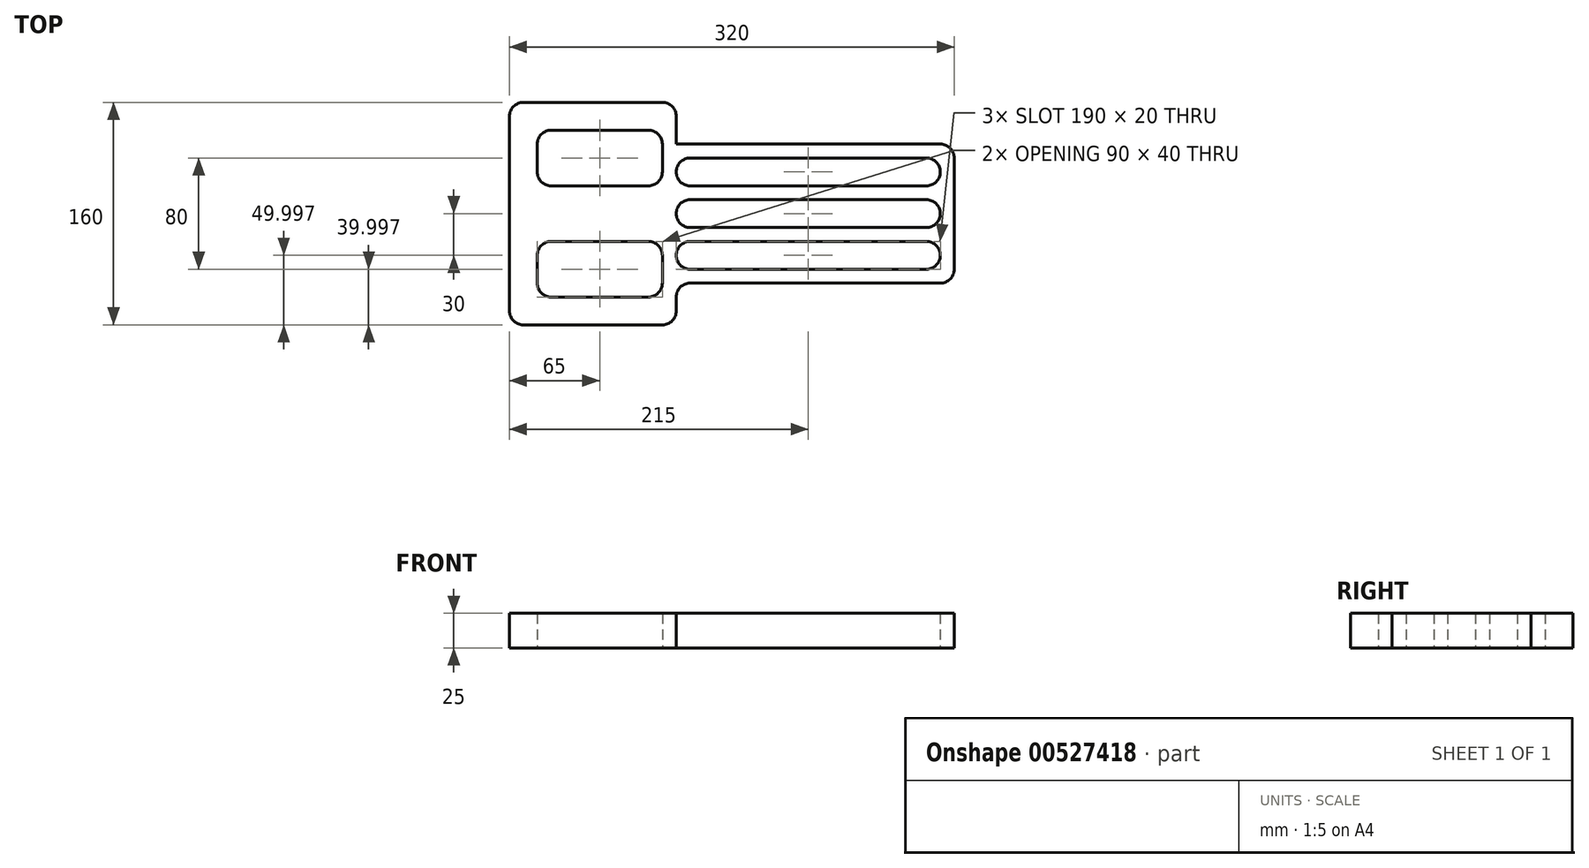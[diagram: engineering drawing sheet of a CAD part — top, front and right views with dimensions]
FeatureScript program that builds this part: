
annotation { "Feature Type Name" : "Feature", "Feature Type Description" : "" }
export const myFeature = defineFeature(function(context is Context, id is Id, definition is map)
    precondition{}
    {
        {
            var Q0;
            Q0=qCreatedBy(makeId("Top.planeOp"),FACE);
            var sketch = newSketch(context, id + "F0", { "sketchPlane" : qUnion([Q0])});
            skLineSegment(sketch, "E0", {"start": v(-100, 104.57) * mm, "end": v(0, 104.57) * mm});
            skLineSegment(sketch, "E1", {"start": v(-110, 94.57) * mm, "end": v(-110, -45.43) * mm});
            skLineSegment(sketch, "E2", {"start": v(-100, -55.43) * mm, "end": v(0, -55.43) * mm});
            skLineSegment(sketch, "E3", {"start": v(10, 94.57) * mm, "end": v(10, 74.57) * mm});
            skLineSegment(sketch, "E4", {"start": v(10, -45.43) * mm, "end": v(10, -35.43) * mm});
            skLineSegment(sketch, "E5", {"start": v(20, -25.43) * mm, "end": v(200, -25.43) * mm});
            skLineSegment(sketch, "E6", {"start": v(10, 74.57) * mm, "end": v(200, 74.57) * mm});
            skLineSegment(sketch, "E7", {"start": v(210, 64.57) * mm, "end": v(210, -15.43) * mm});
            skLineSegment(sketch, "E8.bottom", {"start": v(190, 44.57) * mm, "end": v(20, 44.57) * mm});
            skLineSegment(sketch, "E8.top", {"start": v(190, 64.57) * mm, "end": v(20, 64.57) * mm});
            skLineSegment(sketch, "E8.left", {"start": v(200, 54.57) * mm, "end": v(200, 54.57) * mm});
            skLineSegment(sketch, "E8.right", {"start": v(10, 54.57) * mm, "end": v(10, 54.57) * mm});
            skPoint(sketch, "E8.middle", {"position": v(105, 54.57) * mm});
            skLineSegment(sketch, "E9.bottom", {"start": v(190, 14.57) * mm, "end": v(20, 14.57) * mm});
            skLineSegment(sketch, "E9.top", {"start": v(190, 34.57) * mm, "end": v(20, 34.57) * mm});
            skLineSegment(sketch, "E9.left", {"start": v(200, 24.57) * mm, "end": v(200, 24.57) * mm});
            skLineSegment(sketch, "E9.right", {"start": v(10, 24.57) * mm, "end": v(10, 24.57) * mm});
            skPoint(sketch, "E9.middle", {"position": v(105, 24.57) * mm});
            skLineSegment(sketch, "E10.bottom", {"start": v(190, -15.43) * mm, "end": v(20, -15.43) * mm});
            skLineSegment(sketch, "E10.top", {"start": v(190, 4.57) * mm, "end": v(20, 4.57) * mm});
            skLineSegment(sketch, "E10.left", {"start": v(200, -5.43) * mm, "end": v(200, -5.43) * mm});
            skLineSegment(sketch, "E10.right", {"start": v(10, -5.43) * mm, "end": v(10, -5.43) * mm});
            skPoint(sketch, "E10.middle", {"position": v(105, -5.43) * mm});
            skLineSegment(sketch, "E11.bottom", {"start": v(-10, 84.57) * mm, "end": v(-80, 84.57) * mm});
            skLineSegment(sketch, "E11.top", {"start": v(-10, 44.57) * mm, "end": v(-80, 44.57) * mm});
            skLineSegment(sketch, "E11.left", {"start": v(0, 74.57) * mm, "end": v(0, 54.57) * mm});
            skLineSegment(sketch, "E11.right", {"start": v(-90, 74.57) * mm, "end": v(-90, 54.57) * mm});
            skPoint(sketch, "E11.middle", {"position": v(-45, 64.57) * mm});
            skLineSegment(sketch, "E12.bottom", {"start": v(-10, 4.57) * mm, "end": v(-80, 4.57) * mm});
            skLineSegment(sketch, "E12.top", {"start": v(-10, -35.43) * mm, "end": v(-80, -35.43) * mm});
            skLineSegment(sketch, "E12.left", {"start": v(0, -5.43) * mm, "end": v(0, -25.43) * mm});
            skLineSegment(sketch, "E12.right", {"start": v(-90, -5.43) * mm, "end": v(-90, -25.43) * mm});
            skPoint(sketch, "E12.middle", {"position": v(-45, -15.43) * mm});
            skPoint(sketch, "E13.visualSharp", {"position": v(10, 64.57) * mm});
            skArc(sketch, "E13.filletArc", {"start": v(20, 64.57) * mm, "mid": v(12.93, 61.64) * mm, "end": v(10, 54.57) * mm});
            skPoint(sketch, "E14.visualSharp", {"position": v(10, 44.57) * mm});
            skArc(sketch, "E14.filletArc", {"start": v(10, 54.57) * mm, "mid": v(12.93, 47.5) * mm, "end": v(20, 44.57) * mm});
            skPoint(sketch, "E15.visualSharp", {"position": v(10, 34.57) * mm});
            skArc(sketch, "E15.filletArc", {"start": v(20, 34.57) * mm, "mid": v(12.93, 31.64) * mm, "end": v(10, 24.57) * mm});
            skPoint(sketch, "E16.visualSharp", {"position": v(10, 14.57) * mm});
            skArc(sketch, "E16.filletArc", {"start": v(10, 24.57) * mm, "mid": v(12.93, 17.5) * mm, "end": v(20, 14.57) * mm});
            skPoint(sketch, "E17.visualSharp", {"position": v(10, 4.57) * mm});
            skArc(sketch, "E17.filletArc", {"start": v(20, 4.57) * mm, "mid": v(12.93, 1.64) * mm, "end": v(10, -5.43) * mm});
            skPoint(sketch, "E18.visualSharp", {"position": v(10, -15.43) * mm});
            skArc(sketch, "E18.filletArc", {"start": v(10, -5.43) * mm, "mid": v(12.93, -12.5) * mm, "end": v(20, -15.43) * mm});
            skPoint(sketch, "E19.visualSharp", {"position": v(200, 4.57) * mm});
            skArc(sketch, "E19.filletArc", {"start": v(200, -5.43) * mm, "mid": v(197.07, 1.64) * mm, "end": v(190, 4.57) * mm});
            skPoint(sketch, "E20.visualSharp", {"position": v(200, -15.43) * mm});
            skArc(sketch, "E20.filletArc", {"start": v(190, -15.43) * mm, "mid": v(197.07, -12.5) * mm, "end": v(200, -5.43) * mm});
            skPoint(sketch, "E21.visualSharp", {"position": v(200, 34.57) * mm});
            skArc(sketch, "E21.filletArc", {"start": v(200, 24.57) * mm, "mid": v(197.07, 31.64) * mm, "end": v(190, 34.57) * mm});
            skPoint(sketch, "E22.visualSharp", {"position": v(200, 14.57) * mm});
            skArc(sketch, "E22.filletArc", {"start": v(190, 14.57) * mm, "mid": v(197.07, 17.5) * mm, "end": v(200, 24.57) * mm});
            skPoint(sketch, "E23.visualSharp", {"position": v(200, 64.57) * mm});
            skArc(sketch, "E23.filletArc", {"start": v(200, 54.57) * mm, "mid": v(197.07, 61.64) * mm, "end": v(190, 64.57) * mm});
            skPoint(sketch, "E24.visualSharp", {"position": v(200, 44.57) * mm});
            skArc(sketch, "E24.filletArc", {"start": v(190, 44.57) * mm, "mid": v(197.07, 47.5) * mm, "end": v(200, 54.57) * mm});
            skPoint(sketch, "E25.visualSharp", {"position": v(210, 74.57) * mm});
            skArc(sketch, "E25.filletArc", {"start": v(210, 64.57) * mm, "mid": v(207.07, 71.64) * mm, "end": v(200, 74.57) * mm});
            skPoint(sketch, "E26.visualSharp", {"position": v(210, -25.43) * mm});
            skArc(sketch, "E26.filletArc", {"start": v(200, -25.43) * mm, "mid": v(207.07, -22.5) * mm, "end": v(210, -15.43) * mm});
            skPoint(sketch, "E27.visualSharp", {"position": v(10, -25.43) * mm});
            skArc(sketch, "E27.filletArc", {"start": v(20, -25.43) * mm, "mid": v(12.93, -28.36) * mm, "end": v(10, -35.43) * mm});
            skPoint(sketch, "E28.visualSharp", {"position": v(10, -55.43) * mm});
            skArc(sketch, "E28.filletArc", {"start": v(0, -55.43) * mm, "mid": v(7.07, -52.5) * mm, "end": v(10, -45.43) * mm});
            skPoint(sketch, "E29.visualSharp", {"position": v(-110, -55.43) * mm});
            skArc(sketch, "E29.filletArc", {"start": v(-110, -45.43) * mm, "mid": v(-107.07, -52.5) * mm, "end": v(-100, -55.43) * mm});
            skPoint(sketch, "E30.visualSharp", {"position": v(-90, -35.43) * mm});
            skArc(sketch, "E30.filletArc", {"start": v(-90, -25.43) * mm, "mid": v(-87.07, -32.5) * mm, "end": v(-80, -35.43) * mm});
            skPoint(sketch, "E31.visualSharp", {"position": v(-90, 4.57) * mm});
            skArc(sketch, "E31.filletArc", {"start": v(-80, 4.57) * mm, "mid": v(-87.07, 1.64) * mm, "end": v(-90, -5.43) * mm});
            skPoint(sketch, "E32.visualSharp", {"position": v(0, 4.57) * mm});
            skArc(sketch, "E32.filletArc", {"start": v(0, -5.43) * mm, "mid": v(-2.93, 1.64) * mm, "end": v(-10, 4.57) * mm});
            skPoint(sketch, "E33.visualSharp", {"position": v(0, -35.43) * mm});
            skArc(sketch, "E33.filletArc", {"start": v(-10, -35.43) * mm, "mid": v(-2.93, -32.5) * mm, "end": v(0, -25.43) * mm});
            skPoint(sketch, "E34.visualSharp", {"position": v(-110, 104.57) * mm});
            skArc(sketch, "E34.filletArc", {"start": v(-100, 104.57) * mm, "mid": v(-107.07, 101.64) * mm, "end": v(-110, 94.57) * mm});
            skPoint(sketch, "E35.visualSharp", {"position": v(-90, 84.57) * mm});
            skArc(sketch, "E35.filletArc", {"start": v(-80, 84.57) * mm, "mid": v(-87.07, 81.64) * mm, "end": v(-90, 74.57) * mm});
            skPoint(sketch, "E36.visualSharp", {"position": v(-90, 44.57) * mm});
            skArc(sketch, "E36.filletArc", {"start": v(-90, 54.57) * mm, "mid": v(-87.07, 47.5) * mm, "end": v(-80, 44.57) * mm});
            skPoint(sketch, "E37.visualSharp", {"position": v(0, 44.57) * mm});
            skArc(sketch, "E37.filletArc", {"start": v(-10, 44.57) * mm, "mid": v(-2.93, 47.5) * mm, "end": v(0, 54.57) * mm});
            skPoint(sketch, "E38.visualSharp", {"position": v(0, 84.57) * mm});
            skArc(sketch, "E38.filletArc", {"start": v(0, 74.57) * mm, "mid": v(-2.93, 81.64) * mm, "end": v(-10, 84.57) * mm});
            skPoint(sketch, "E39.visualSharp", {"position": v(10, 104.57) * mm});
            skArc(sketch, "E39.filletArc", {"start": v(10, 94.57) * mm, "mid": v(7.07, 101.64) * mm, "end": v(0, 104.57) * mm});
            skSolve(sketch);
        }
        {
            var Q0;
            Q0=makeQuery(id+"F0.imprint","IMPRINT",FACE,{"disambiguationData":[TD([[makeQuery(id+"F0.imprint","IMPRINT",EDGE,{"derivedFrom":sQuery(id+"F0.wireOp",EDGE,"E0")}),-1.0]])]});
            extrude(context, id + "F1", {"entities" : qUnion([Q0]), "depth" : 25 * mm, "offsetDistance" : 25 * mm});
        }
    });
